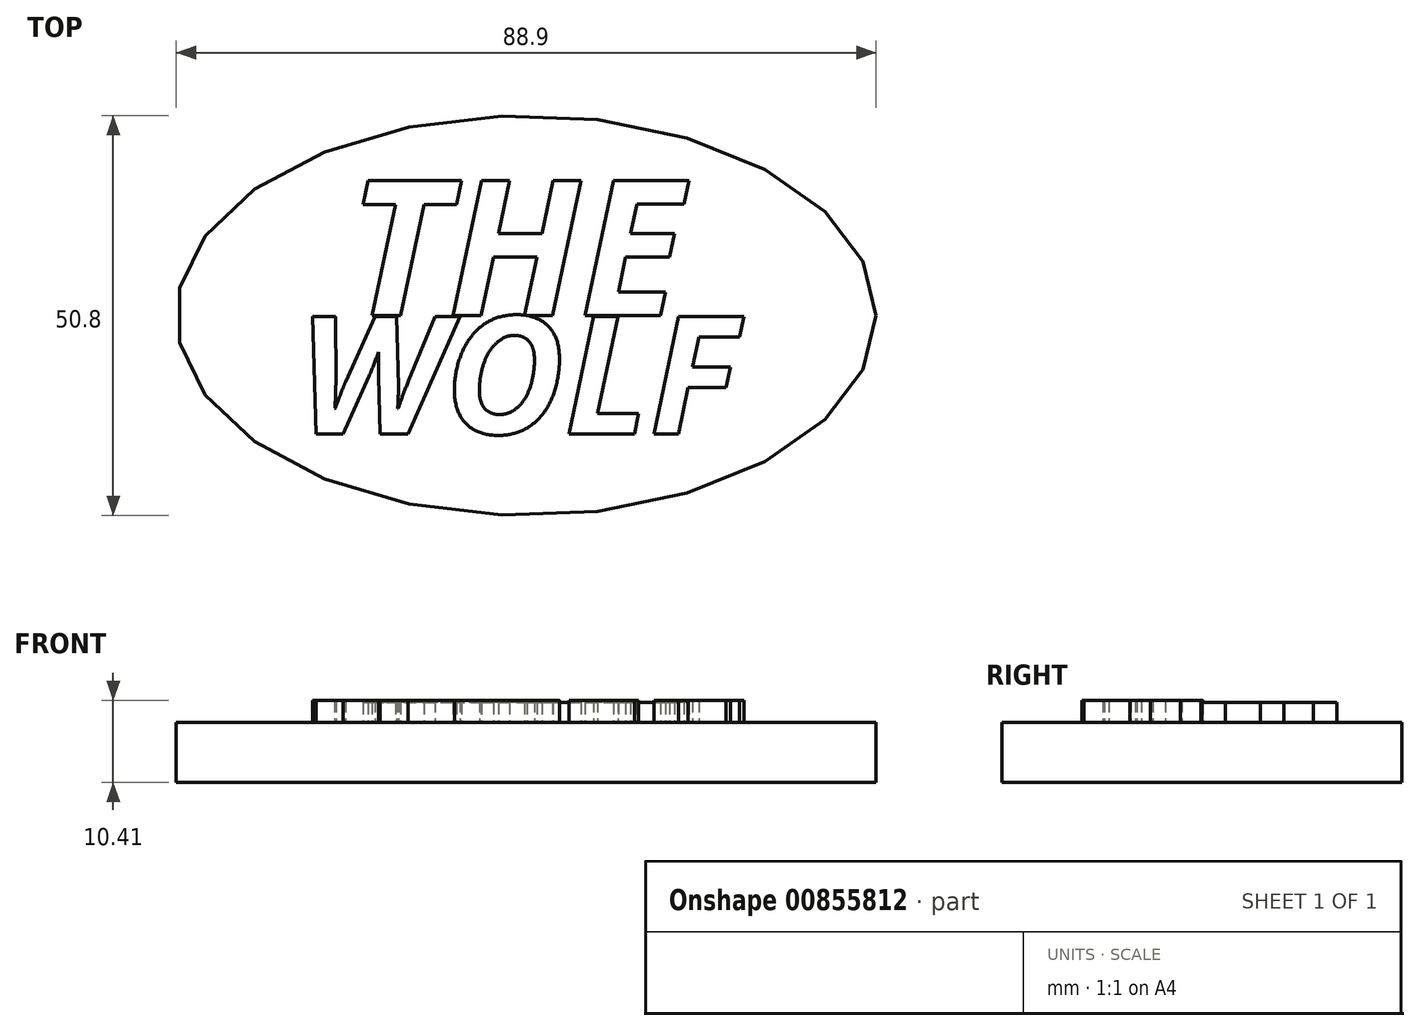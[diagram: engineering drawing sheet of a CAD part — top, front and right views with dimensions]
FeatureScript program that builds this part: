
annotation { "Feature Type Name" : "Feature", "Feature Type Description" : "" }
export const myFeature = defineFeature(function(context is Context, id is Id, definition is map)
    precondition{}
    {
        {
            var Q0;
            Q0=qCreatedBy(makeId("Top.planeOp"),FACE);
            var sketch = newSketch(context, id + "F0", { "sketchPlane" : qUnion([Q0])});
            skEllipse(sketch, "E0", {"center": v(0, 0) * mm, "majorRadius": 44.45 * mm, "minorRadius": 25.4 * mm, "majorAxis": v(1, 0)});
            skSolve(sketch);
        }
        {
            var Q0;
            Q0=makeQuery(id+"F0.imprint","IMPRINT",FACE,{"disambiguationData":[TD([[makeQuery(id+"F0.imprint","IMPRINT",EDGE,{"derivedFrom":sQuery(id+"F0.wireOp",EDGE,"E0")}),1.0]])]});
            extrude(context, id + "F1", {"entities" : qUnion([Q0]), "depth" : 7.62 * mm, "offsetDistance" : 25.4 * mm});
        }
        {
            var Q0;
            Q0=makeQuery(id+"F1.opExtrude","CAP_FACE",FACE,{"disambiguationData":[OSD([sQuery(id+"F0.wireOp",EDGE,"E0")])],"isStart":false});
            var sketch = newSketch(context, id + "F2", { "sketchPlane" : qUnion([Q0])});
            skText(sketch, "E1", { "text": "THE", "fontName": "OpenSans-BoldItalic.ttf"});
            const initialGuessF2  = {"E1": [-0.02267, 0, 1, 0, 0.01728]};
            skSetInitialGuess(sketch, initialGuessF2);
            skSolve(sketch);
        }
        {
            var Q0;
            Q0=makeQuery(id+"F2.imprint","IMPRINT",FACE,{"disambiguationData":[TD([[makeQuery(id+"F2.imprint","IMPRINT",EDGE,{"derivedFrom":sQuery(id+"F2.wireOp",EDGE,"E1.sketch_text.stroke-0")}),1.0]])]});
            var sketch = newSketch(context, id + "F3", { "sketchPlane" : qUnion([Q0])});
            skText(sketch, "E2", { "text": "WOLF", "fontName": "OpenSans-BoldItalic.ttf"});
            const initialGuessF3  = {"E2": [-0.02903, -0.01503, 1, 0, 0.01503]};
            skSetInitialGuess(sketch, initialGuessF3);
            skSolve(sketch);
        }
        {
            var Q0;
            Q0 = qSketchRegion(id + "F2", true);
            extrude(context, id + "F4", {"entities" : qUnion([Q0]), "operationType" : NewBodyOperationType.ADD, "depth" : 2.54 * mm, "offsetDistance" : 25.4 * mm});
        }
        {
            var Q0;
            Q0 = qSketchRegion(id + "F3", true);
            extrude(context, id + "F5", {"entities" : qUnion([Q0]), "operationType" : NewBodyOperationType.ADD, "depth" : 2.8 * mm, "offsetDistance" : 25.4 * mm});
        }
    });
